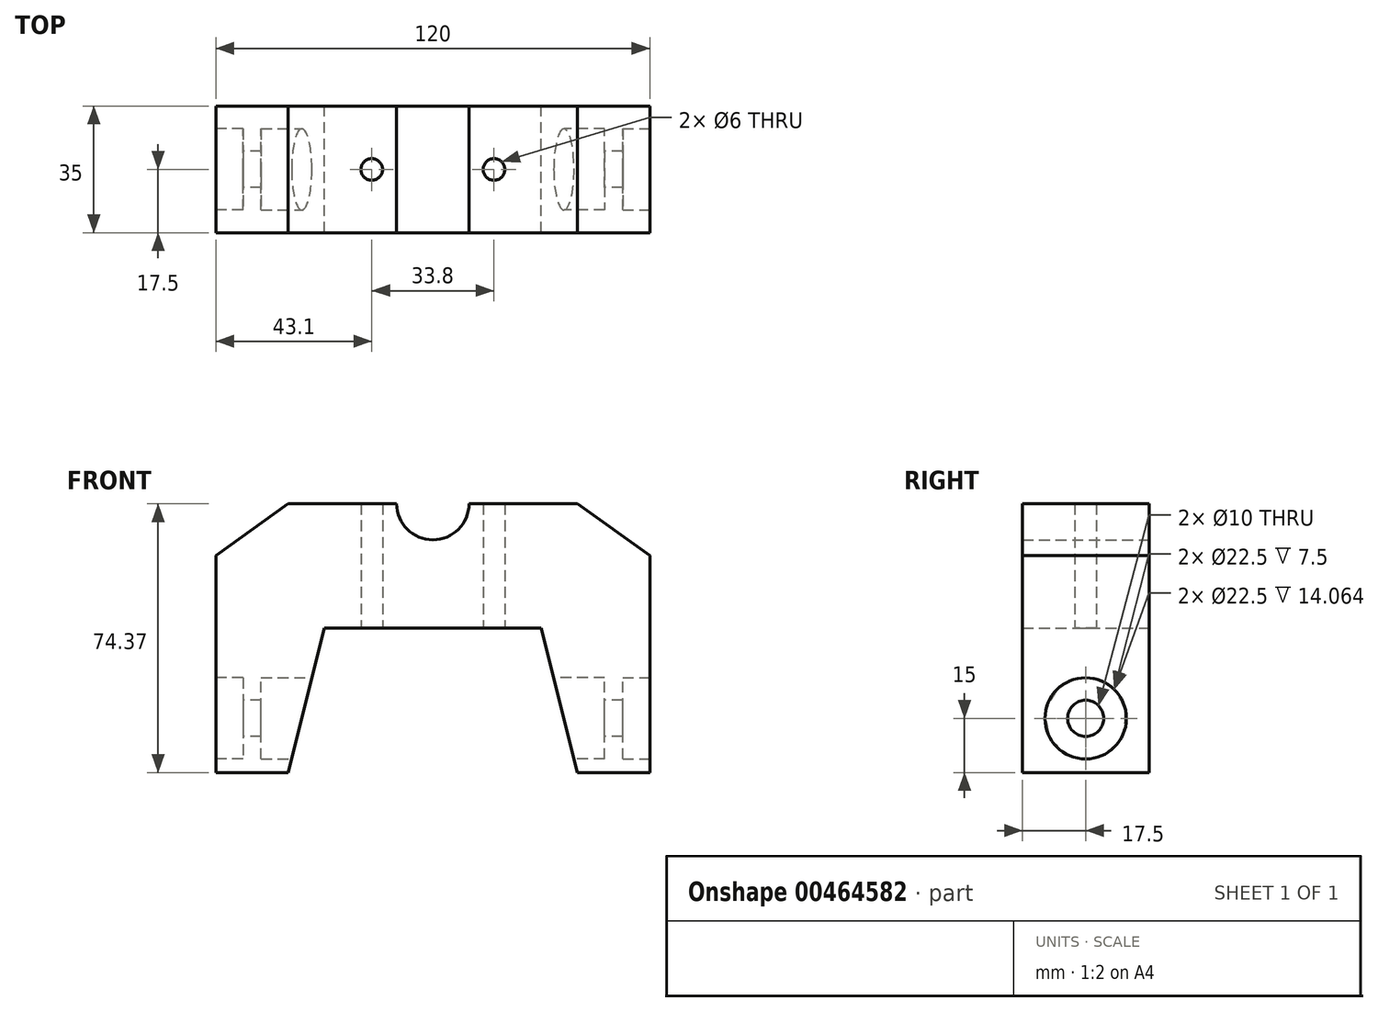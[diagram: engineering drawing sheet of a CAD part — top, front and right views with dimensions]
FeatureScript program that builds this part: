
annotation { "Feature Type Name" : "Feature", "Feature Type Description" : "" }
export const myFeature = defineFeature(function(context is Context, id is Id, definition is map)
    precondition{}
    {
        {
            var Q0;
            Q0=qCreatedBy(makeId("Front.planeOp"),FACE);
            var sketch = newSketch(context, id + "F0", { "sketchPlane" : qUnion([Q0])});
            skLineSegment(sketch, "E0", {"start": v(0, 0) * mm, "end": v(60, 0) * mm, "construction": true});
            skLineSegment(sketch, "E1", {"start": v(0, 0) * mm, "end": v(0, 19.37) * mm, "construction": true});
            skLineSegment(sketch, "E2", {"start": v(0, 0) * mm, "end": v(-60, 0) * mm, "construction": true});
            skLineSegment(sketch, "E3", {"start": v(0, 0) * mm, "end": v(0, -15) * mm, "construction": true});
            skLineSegment(sketch, "E4", {"start": v(-60, 5) * mm, "end": v(-60, 0) * mm});
            skLineSegment(sketch, "E5", {"start": v(-60, 0) * mm, "end": v(-60, -55) * mm});
            skLineSegment(sketch, "E6", {"start": v(60, 0) * mm, "end": v(60, -55) * mm});
            skLineSegment(sketch, "E7", {"start": v(60, 0) * mm, "end": v(60, 5) * mm});
            skArc(sketch, "E8", {"start": v(-10, 19.37) * mm, "mid": v(0, 9.37) * mm, "end": v(10, 19.37) * mm});
            skLineSegment(sketch, "E9", {"start": v(-60, -55) * mm, "end": v(-40, -55) * mm});
            skLineSegment(sketch, "E10", {"start": v(60, -55) * mm, "end": v(40, -55) * mm});
            skLineSegment(sketch, "E11", {"start": v(0, -15) * mm, "end": v(-30, -15) * mm});
            skLineSegment(sketch, "E12", {"start": v(0, -15) * mm, "end": v(30, -15) * mm});
            skLineSegment(sketch, "E13", {"start": v(-40, -55) * mm, "end": v(-30, -15) * mm});
            skLineSegment(sketch, "E14", {"start": v(30, -15) * mm, "end": v(40, -55) * mm});
            skLineSegment(sketch, "E15", {"start": v(-10, 19.37) * mm, "end": v(-40, 19.37) * mm});
            skLineSegment(sketch, "E16", {"start": v(-40, 19.37) * mm, "end": v(-60, 5) * mm});
            skLineSegment(sketch, "E17", {"start": v(10, 19.37) * mm, "end": v(40, 19.37) * mm});
            skLineSegment(sketch, "E18", {"start": v(40, 19.37) * mm, "end": v(60, 5) * mm});
            skSolve(sketch);
        }
        {
            var Q0;
            Q0=qSketchRegion(id+"F0",true);
            extrude(context, id + "F1", {"entities" : qUnion([Q0]), "depth" : 35 * mm, "offsetDistance" : 25 * mm});
        }
        {
            var Q0;
            Q0=makeQuery(id+"F1.opExtrude","SWEPT_FACE",FACE,{"disambiguationData":[OSD([sQuery(id+"F0.wireOp",EDGE,"E11"),sQuery(id+"F0.wireOp",EDGE,"E12")])]});
            var sketch = newSketch(context, id + "F2", { "sketchPlane" : qUnion([Q0])});
            skCircle(sketch, "E19", {"center": v(-16.9, 17.5) * mm, "radius": 3 * mm});
            skLineSegment(sketch, "E20", {"start": v(-16.9, 17.5) * mm, "end": v(16.9, 17.5) * mm, "construction": true});
            skCircle(sketch, "E21", {"center": v(16.9, 17.5) * mm, "radius": 3 * mm});
            skSolve(sketch);
        }
        {
            var Q0;
            Q0=qSketchRegion(id+"F2",true);
            extrude(context, id + "F3", {"entities" : qUnion([Q0]), "operationType" : NewBodyOperationType.REMOVE, "endBound" : BoundingType.THROUGH_ALL, "oppositeDirection" : true, "depth" : 25 * mm, "offsetDistance" : 25 * mm});
        }
        {
            var Q0;
            Q0=makeQuery(id+"F1.opExtrude","SWEPT_FACE",FACE,{"disambiguationData":[OSD([sQuery(id+"F0.wireOp",EDGE,"E4"),sQuery(id+"F0.wireOp",EDGE,"E5")])]});
            var sketch = newSketch(context, id + "F4", { "sketchPlane" : qUnion([Q0])});
            skCircle(sketch, "E22", {"center": v(17.5, -40) * mm, "radius": 5 * mm});
            skSolve(sketch);
        }
        {
            var Q0;
            Q0=qSketchRegion(id+"F4",true);
            extrude(context, id + "F5", {"entities" : qUnion([Q0]), "operationType" : NewBodyOperationType.REMOVE, "endBound" : BoundingType.THROUGH_ALL, "oppositeDirection" : true, "depth" : 25 * mm, "offsetDistance" : 25 * mm});
        }
        {
            var Q0;
            Q0=makeQuery(id+"F1.opExtrude","SWEPT_FACE",FACE,{"disambiguationData":[OSD([sQuery(id+"F0.wireOp",EDGE,"E4"),sQuery(id+"F0.wireOp",EDGE,"E5")])]});
            var sketch = newSketch(context, id + "F6", { "sketchPlane" : qUnion([Q0])});
            skCircle(sketch, "E23", {"center": v(17.5, -40) * mm, "radius": 11.25 * mm});
            skSolve(sketch);
        }
        {
            var Q0;
            Q0 = qSketchRegion(id + "F6", true);
            extrude(context, id + "F7", {"entities" : qUnion([Q0]), "operationType" : NewBodyOperationType.REMOVE, "oppositeDirection" : true, "depth" : 7.5 * mm, "offsetDistance" : 25 * mm});
        }
        {
            var Q0;
            Q0=makeQuery(id+"F1.opExtrude","SWEPT_FACE",FACE,{"disambiguationData":[OSD([sQuery(id+"F0.wireOp",EDGE,"E6"),sQuery(id+"F0.wireOp",EDGE,"E7")])]});
            var sketch = newSketch(context, id + "F8", { "sketchPlane" : qUnion([Q0])});
            skCircle(sketch, "E24", {"center": v(-17.5, -40) * mm, "radius": 11.25 * mm});
            skSolve(sketch);
        }
        {
            var Q0;
            Q0 = qSketchRegion(id + "F8", true);
            extrude(context, id + "F9", {"entities" : qUnion([Q0]), "operationType" : NewBodyOperationType.REMOVE, "oppositeDirection" : true, "depth" : 7.5 * mm, "offsetDistance" : 25 * mm});
        }
        {
            var Q0;
            Q0=qCreatedBy(makeId("Right.planeOp"),FACE);
            var sketch = newSketch(context, id + "F10", { "sketchPlane" : qUnion([Q0])});
            skCircle(sketch, "E25", {"center": v(-17.5, -40) * mm, "radius": 11.25 * mm});
            skSolve(sketch);
        }
        {
            var Q0;
            Q0 = qSketchRegion(id + "F10", true);
            extrude(context, id + "F11", {"entities" : qUnion([Q0]), "operationType" : NewBodyOperationType.REMOVE, "oppositeDirection" : true, "depth" : 47.5 * mm, "offsetDistance" : 25 * mm});
        }
        {
            var Q0;
            Q0=qCreatedBy(makeId("Right.planeOp"),FACE);
            var sketch = newSketch(context, id + "F12", { "sketchPlane" : qUnion([Q0])});
            skCircle(sketch, "E26", {"center": v(-17.5, -40) * mm, "radius": 11.25 * mm});
            skSolve(sketch);
        }
        {
            var Q0;
            Q0 = qSketchRegion(id + "F12", true);
            extrude(context, id + "F13", {"entities" : qUnion([Q0]), "operationType" : NewBodyOperationType.REMOVE, "depth" : 47.5 * mm, "offsetDistance" : 25 * mm});
        }
    });
